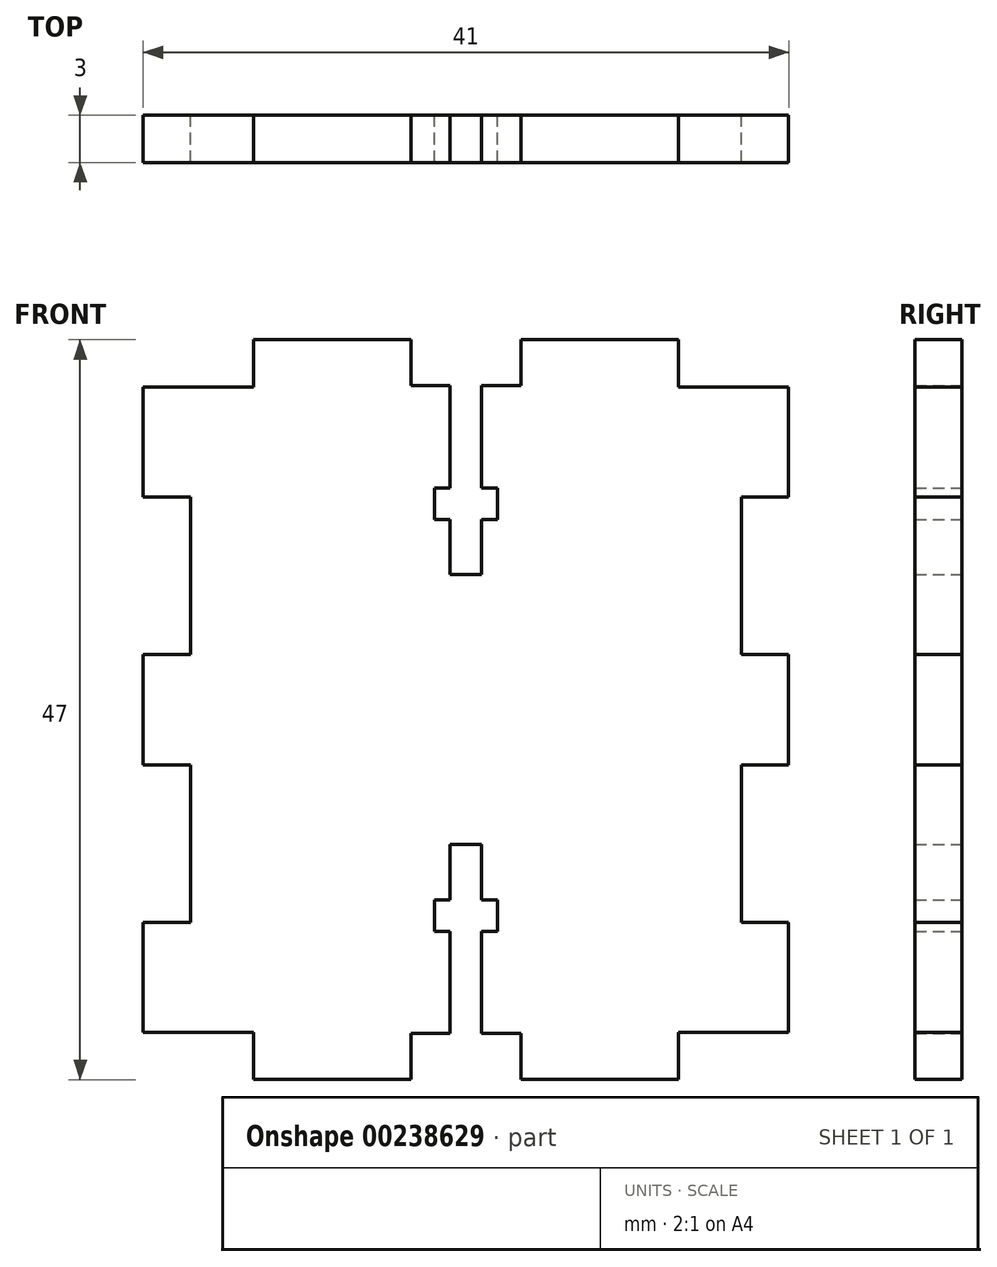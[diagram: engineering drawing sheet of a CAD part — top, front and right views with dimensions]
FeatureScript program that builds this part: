
annotation { "Feature Type Name" : "Feature", "Feature Type Description" : "" }
export const myFeature = defineFeature(function(context is Context, id is Id, definition is map)
    precondition{}
    {
        {
            var Q0;
            Q0=qCreatedBy(makeId("Front.planeOp"),FACE);
            var sketch = newSketch(context, id + "F0", { "sketchPlane" : qUnion([Q0])});
            skLineSegment(sketch, "E0.bottom", {"start": v(13.67, 23.3) * mm, "end": v(3.67, 23.3) * mm});
            skLineSegment(sketch, "E0.top", {"start": v(13.67, -23.7) * mm, "end": v(3.67, -23.7) * mm});
            skLineSegment(sketch, "E0.right", {"start": v(-20.33, 20.3) * mm, "end": v(-20.33, 13.3) * mm});
            skPoint(sketch, "E0.middle", {"position": v(0.17, -0.2) * mm});
            skLineSegment(sketch, "E1.top", {"start": v(-20.33, 20.3) * mm, "end": v(-13.33, 20.3) * mm});
            skLineSegment(sketch, "E1.right", {"start": v(-13.33, 23.3) * mm, "end": v(-13.33, 20.3) * mm});
            skPoint(sketch, "E1.middle", {"position": v(-16.83, 21.8) * mm});
            skPoint(sketch, "E2.orphan", {"position": v(-20.33, 23.3) * mm});
            skLineSegment(sketch, "E3.top", {"start": v(-3.33, 20.37) * mm, "end": v(-0.83, 20.37) * mm});
            skLineSegment(sketch, "E3.left", {"start": v(-3.33, 23.3) * mm, "end": v(-3.33, 20.37) * mm});
            skLineSegment(sketch, "E4.MirrorCS", {"start": v(13.67, 23.3) * mm, "end": v(13.67, 20.3) * mm});
            skLineSegment(sketch, "E5.MirrorCS", {"start": v(3.67, 23.3) * mm, "end": v(3.67, 20.37) * mm});
            skLineSegment(sketch, "E6.MirrorCS", {"start": v(20.67, 20.3) * mm, "end": v(13.67, 20.3) * mm});
            skPoint(sketch, "E7.MirrorP", {"position": v(20.67, 23.3) * mm});
            skPoint(sketch, "E8.MirrorP", {"position": v(17.17, 21.8) * mm});
            skLineSegment(sketch, "E9.MirrorCS", {"start": v(3.67, 20.37) * mm, "end": v(1.17, 20.37) * mm});
            skLineSegment(sketch, "E10.MirrorCS", {"start": v(3.67, -23.7) * mm, "end": v(3.67, -20.78) * mm});
            skLineSegment(sketch, "E11.MirrorCS", {"start": v(-3.33, -23.7) * mm, "end": v(-3.33, -20.78) * mm});
            skLineSegment(sketch, "E12.MirrorCS", {"start": v(-13.33, -23.7) * mm, "end": v(-13.33, -20.7) * mm});
            skLineSegment(sketch, "E13.MirrorCS", {"start": v(13.67, -23.7) * mm, "end": v(13.67, -20.7) * mm});
            skLineSegment(sketch, "E14.MirrorCS", {"start": v(-20.33, -20.7) * mm, "end": v(-13.33, -20.7) * mm});
            skLineSegment(sketch, "E15.MirrorCS", {"start": v(20.67, -20.7) * mm, "end": v(13.67, -20.7) * mm});
            skLineSegment(sketch, "E16.MirrorCS", {"start": v(-3.33, -20.78) * mm, "end": v(-0.83, -20.78) * mm});
            skPoint(sketch, "E17.MirrorP", {"position": v(17.17, -22.2) * mm});
            skLineSegment(sketch, "E18.MirrorCS", {"start": v(3.67, -20.78) * mm, "end": v(1.17, -20.78) * mm});
            skPoint(sketch, "E19.MirrorP", {"position": v(-20.33, -23.7) * mm});
            skPoint(sketch, "E20.MirrorP", {"position": v(20.67, -23.7) * mm});
            skPoint(sketch, "E21.MirrorP", {"position": v(-16.83, -22.2) * mm});
            skLineSegment(sketch, "E22.trimOffspring", {"start": v(-3.33, -23.7) * mm, "end": v(-13.33, -23.7) * mm});
            skPoint(sketch, "E23.MirrorCS.end.orphan", {"position": v(0.17, -23.7) * mm});
            skLineSegment(sketch, "E24.trimOffspring", {"start": v(-3.33, 23.3) * mm, "end": v(-13.33, 23.3) * mm});
            skPoint(sketch, "E25.MirrorCS.start.orphan", {"position": v(0.17, 23.3) * mm});
            skLineSegment(sketch, "E26.bottom", {"start": v(-20.33, 13.3) * mm, "end": v(-17.33, 13.3) * mm});
            skLineSegment(sketch, "E26.top", {"start": v(-20.33, 3.3) * mm, "end": v(-17.33, 3.3) * mm});
            skLineSegment(sketch, "E26.right", {"start": v(-17.33, 13.3) * mm, "end": v(-17.33, 3.3) * mm});
            skLineSegment(sketch, "E27.trimOffspring", {"start": v(-20.33, 3.3) * mm, "end": v(-20.33, -3.7) * mm});
            skLineSegment(sketch, "E28.MirrorCS", {"start": v(20.67, 3.3) * mm, "end": v(17.67, 3.3) * mm});
            skLineSegment(sketch, "E29.MirrorCS", {"start": v(17.67, 13.3) * mm, "end": v(17.67, 3.3) * mm});
            skLineSegment(sketch, "E30.MirrorCS", {"start": v(20.67, 13.3) * mm, "end": v(17.67, 13.3) * mm});
            skLineSegment(sketch, "E31.MirrorCS", {"start": v(-20.33, -3.7) * mm, "end": v(-17.33, -3.7) * mm});
            skLineSegment(sketch, "E32.MirrorCS", {"start": v(-20.33, -20.7) * mm, "end": v(-20.33, -13.7) * mm});
            skLineSegment(sketch, "E33.MirrorCS", {"start": v(-20.33, -13.7) * mm, "end": v(-17.33, -13.7) * mm});
            skLineSegment(sketch, "E34.MirrorCS", {"start": v(20.67, -3.7) * mm, "end": v(17.67, -3.7) * mm});
            skLineSegment(sketch, "E35.MirrorCS", {"start": v(20.67, -13.7) * mm, "end": v(17.67, -13.7) * mm});
            skLineSegment(sketch, "E36.MirrorCS", {"start": v(17.67, -13.7) * mm, "end": v(17.67, -3.7) * mm});
            skLineSegment(sketch, "E37.MirrorCS", {"start": v(-17.33, -13.7) * mm, "end": v(-17.33, -3.7) * mm});
            skLineSegment(sketch, "E38.trimOffspring", {"start": v(-20.33, 13.3) * mm, "end": v(-20.33, 20.3) * mm});
            skLineSegment(sketch, "E39.trimOffspring", {"start": v(20.67, 13.3) * mm, "end": v(20.67, 20.3) * mm});
            skLineSegment(sketch, "E40.trimOffspring", {"start": v(20.67, 3.3) * mm, "end": v(20.67, -3.7) * mm});
            skPoint(sketch, "E41.MirrorCS.start.orphan", {"position": v(20.67, -20.7) * mm});
            skLineSegment(sketch, "E42.trimOffspring", {"start": v(20.67, -13.7) * mm, "end": v(20.67, -20.7) * mm});
            skLineSegment(sketch, "E43.trimOffspring", {"start": v(-20.33, -13.7) * mm, "end": v(-20.33, -20.7) * mm});
            skLineSegment(sketch, "E44.top", {"start": v(-0.83, 8.37) * mm, "end": v(1.17, 8.37) * mm});
            skLineSegment(sketch, "E44.left", {"start": v(-0.83, 20.37) * mm, "end": v(-0.83, 13.87) * mm});
            skLineSegment(sketch, "E44.right", {"start": v(1.17, 20.37) * mm, "end": v(1.17, 13.87) * mm});
            skLineSegment(sketch, "E45.bottom", {"start": v(-1.83, 13.87) * mm, "end": v(-0.83, 13.87) * mm});
            skLineSegment(sketch, "E45.top", {"start": v(-1.83, 11.87) * mm, "end": v(-0.83, 11.87) * mm});
            skLineSegment(sketch, "E45.left", {"start": v(-1.83, 13.87) * mm, "end": v(-1.83, 11.87) * mm});
            skLineSegment(sketch, "E45.right", {"start": v(2.17, 13.87) * mm, "end": v(2.17, 11.87) * mm});
            skPoint(sketch, "E46.orphan", {"position": v(0.17, 20.37) * mm});
            skLineSegment(sketch, "E47.trimOffspring", {"start": v(1.17, 13.87) * mm, "end": v(2.17, 13.87) * mm});
            skLineSegment(sketch, "E48.trimOffspring", {"start": v(1.17, 11.87) * mm, "end": v(2.17, 11.87) * mm});
            skLineSegment(sketch, "E49.trimOffspring", {"start": v(-0.83, 11.87) * mm, "end": v(-0.83, 8.37) * mm});
            skLineSegment(sketch, "E50.trimOffspring", {"start": v(1.17, 11.87) * mm, "end": v(1.17, 8.37) * mm});
            skLineSegment(sketch, "E51.MirrorCS", {"start": v(-1.83, -14.28) * mm, "end": v(-0.83, -14.28) * mm});
            skLineSegment(sketch, "E52.MirrorCS", {"start": v(-0.83, -8.78) * mm, "end": v(1.17, -8.78) * mm});
            skLineSegment(sketch, "E53.MirrorCS", {"start": v(1.17, -12.28) * mm, "end": v(2.17, -12.28) * mm});
            skLineSegment(sketch, "E54.MirrorCS", {"start": v(-1.83, -12.28) * mm, "end": v(-0.83, -12.28) * mm});
            skLineSegment(sketch, "E55.MirrorCS", {"start": v(1.17, -14.28) * mm, "end": v(2.17, -14.28) * mm});
            skLineSegment(sketch, "E56.MirrorCS", {"start": v(-1.83, -14.28) * mm, "end": v(-1.83, -12.28) * mm});
            skLineSegment(sketch, "E57.MirrorCS", {"start": v(2.17, -14.28) * mm, "end": v(2.17, -12.28) * mm});
            skLineSegment(sketch, "E58.MirrorCS", {"start": v(1.17, -12.28) * mm, "end": v(1.17, -8.78) * mm});
            skPoint(sketch, "E59.MirrorP", {"position": v(0.17, -20.78) * mm});
            skLineSegment(sketch, "E60.MirrorCS", {"start": v(-0.83, -12.28) * mm, "end": v(-0.83, -8.78) * mm});
            skLineSegment(sketch, "E61.MirrorCS", {"start": v(-0.83, -20.78) * mm, "end": v(-0.83, -14.28) * mm});
            skLineSegment(sketch, "E62.MirrorCS", {"start": v(1.17, -20.78) * mm, "end": v(1.17, -14.28) * mm});
            skSolve(sketch);
        }
        {
            var Q0;
            Q0 = qSketchRegion(id + "F0", true);
            extrude(context, id + "F1", {"entities" : qUnion([Q0]), "depth" : 3 * mm, "offsetDistance" : 25 * mm});
        }
    });
